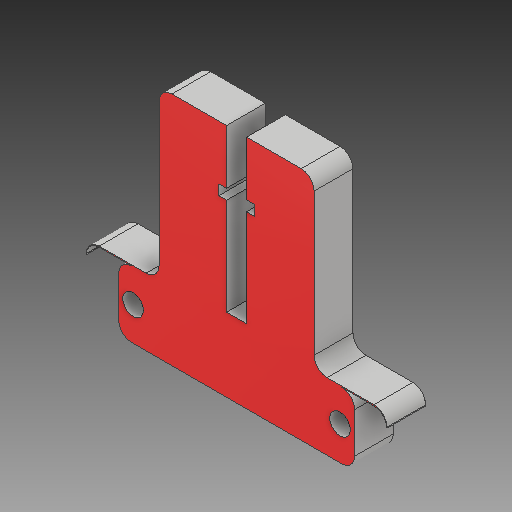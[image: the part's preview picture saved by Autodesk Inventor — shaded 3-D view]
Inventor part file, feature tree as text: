
AUTODESK INVENTOR PART (.ipt)
format: ipt  version: 2018 (Build 220112000, 112)  size: 184,832 bytes
history: native  units: mm
features: sketch x6, other x3
ambient origin geometry x8: Origin, YZ Plane, XZ Plane, XY Plane, X Axis, Y Axis, Z Axis, Center Point
bodies: Solid1 (feature_tree)
feature tree (9):
  other  "Hotend Slide Part 1_MIR.ipt"
  other  "Solid1::Hotend Slide Part 1_MIR.ipt"
  other  "TaggingFeature1"
  sketch  "Sketch1"  dims[d0=10.0mm]
  sketch  "Sketch2"
  sketch  "Sketch3"
  sketch  "Sketch4"
  sketch  "Sketch5"
  sketch  "Sketch6"
